# Revit family: JDRM - Radiant Ceiling Panel
name_source: partatom
category: Mechanical Equipment
units: mm (PartAtom-declared; Revit-internal decimal feet)

## family parameters
Always vertical = Yes
Cut with Voids When Loaded = No
Part Type = Normal
Room Calculation Point = No
Round Connector Dimension = Use Diameter
Shared = No
Work Plane-Based = No

## types (14) — shared parameters
Com_Mark = RP
Com_NeedsData = No
Com_NeedsDisconnect = No
Com_NeedsDrain = No
Com_NeedsDuct = No
Com_NeedsGas = No
Com_NeedsInterlock = No
Com_NeedsPiping = Yes
Com_NeedsPlumbing = No
Com_NeedsPower = No
Com_NeedsSmokeDet = No
Com_NeedsStarter = No
Com_NeedsVent = No
Com_UnitManufacturer = AIRTEX
Com_UnitType = LINEAR EXTRUDED ALUMINUM
Manufacturer = AIRTEX
Mech_ElementTubeSize = 1"
Mech_LoadPerLnFT = 0.0 Btu/h
return connection = 0' - 1"
supply connection = 0' - 1"

## per-type parameters (varying)
| type | MODEL | SIZE | length | width |
| 2x1 |  |  | 20' - 0" | 1' - 0" |
| 1x16 |  |  | 16' - 0" | 1' - 0" |
| 1x11 |  |  | 11' - 0" | 1' - 0" |
| 1x23 | HEF-2 | 12" WIDE | 23' - 3" | 1' - 0" |
| 1x14 |  |  | 14' - 0" | 1' - 0" |
| 8"X5' | KP | KP-50-2 | 5' - 0" | 0' - 8" |
| 8"X22' | HEF-2 | 8"x22' | 22' - 0" | 0' - 8" |
| 8"X14' | HEF-2 | 8"x14' | 14' - 0" | 0' - 8" |
| 1x5 | HEF-2 | 12" WIDE | 5' - 0" | 1' - 0" |
| 1x24 |  |  | 24' - 0" | 1' - 0" |
| 1x25 |  |  | 25' - 0" | 1' - 0" |
| 1x9.8 | HEF-2 | 12" WIDE | 9' - 8" | 1' - 0" |
| 1x8.8 | HEF-2 | 12" WIDE | 8' - 8" | 1' - 0" |
| 1x12.8 | HEF-2 | 12" WIDE | 12' - 9" | 1' - 0" |

## geometry (parser evidence)
native form markers: Blend x4, Sweep x1
no freeform markers — native parametric forms only
